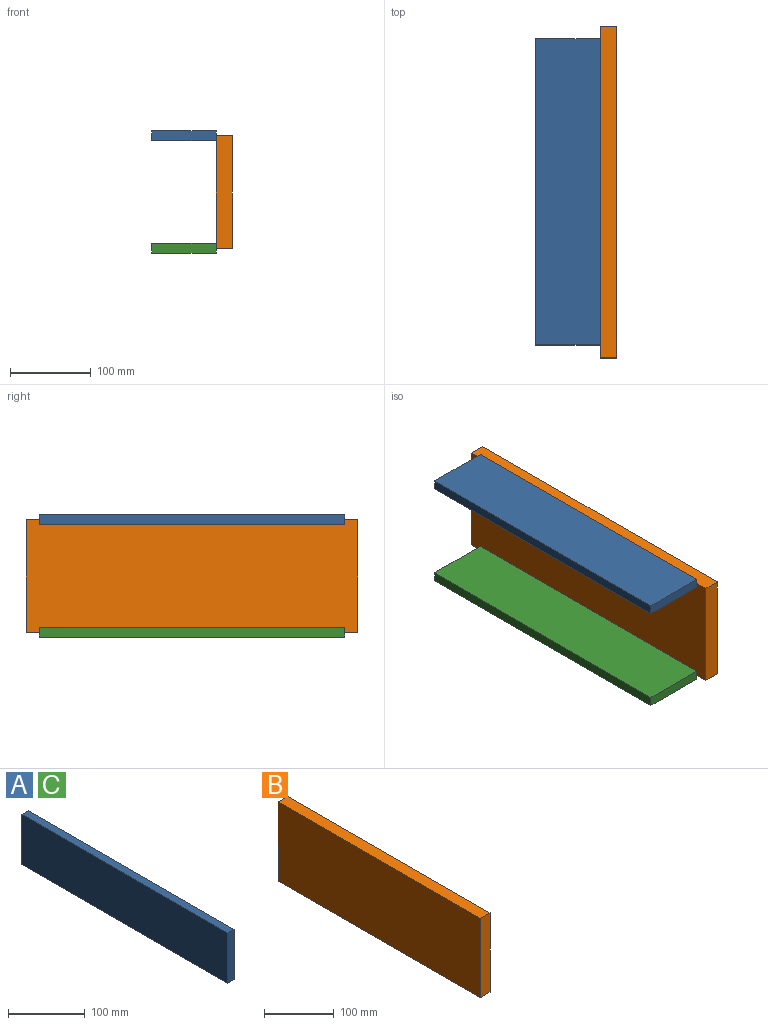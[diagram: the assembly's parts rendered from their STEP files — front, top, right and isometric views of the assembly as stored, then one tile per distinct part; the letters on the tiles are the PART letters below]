
ASSEMBLY  parts=3 mates=2
PART A: 6 faces, bbox 12x378x80 mm
  f0: plane 80x12mm, normal (0,-1,0), area 960mm2, adj f1,f3,f4,f5
  f1: plane 378x12mm, normal (0,0,-1), area 4536mm2, adj f0,f2,f4,f5
  f2: plane 80x12mm, normal (0,1,0), area 960mm2, adj f1,f3,f4,f5
  f3: plane 378x12mm, normal (0,0,1), area 4536mm2, adj f0,f2,f4,f5
  f4: plane 378x80mm, normal (1,0,0), area 30240mm2, adj f0,f1,f2,f3
  f5: plane 378x80mm, normal (-1,0,0), area 30240mm2, adj f0,f1,f2,f3
PART B: 6 faces, bbox 20x410x139 mm
  f0: plane 139x20mm, normal (0,-1,0), area 2780mm2, adj f1,f3,f4,f5
  f1: plane 410x20mm, normal (0,0,-1), area 8200mm2, adj f0,f2,f4,f5
  f2: plane 139x20mm, normal (0,1,0), area 2780mm2, adj f1,f3,f4,f5
  f3: plane 410x20mm, normal (0,0,1), area 8200mm2, adj f0,f2,f4,f5
  f4: plane 410x139mm, normal (1,0,0), area 56990mm2, adj f0,f1,f2,f3
  f5: plane 410x139mm, normal (-1,0,0), area 56990mm2, adj f0,f1,f2,f3
PART C: same geometry as A
PLACE A rot(axis=(0,-1,0),90deg) t=(-40,0,63.5)mm
PLACE B at identity fixed
PLACE C rot(axis=(0,-1,0),90deg) t=(-40,0,-75.5)mm
MATE fastened A.f1 <-> B.f5  axis (1,0,0) through (0,0,69.5)mm
MATE fastened C.f1 <-> B.f5  axis (1,0,0) through (0,0,-69.5)mm
